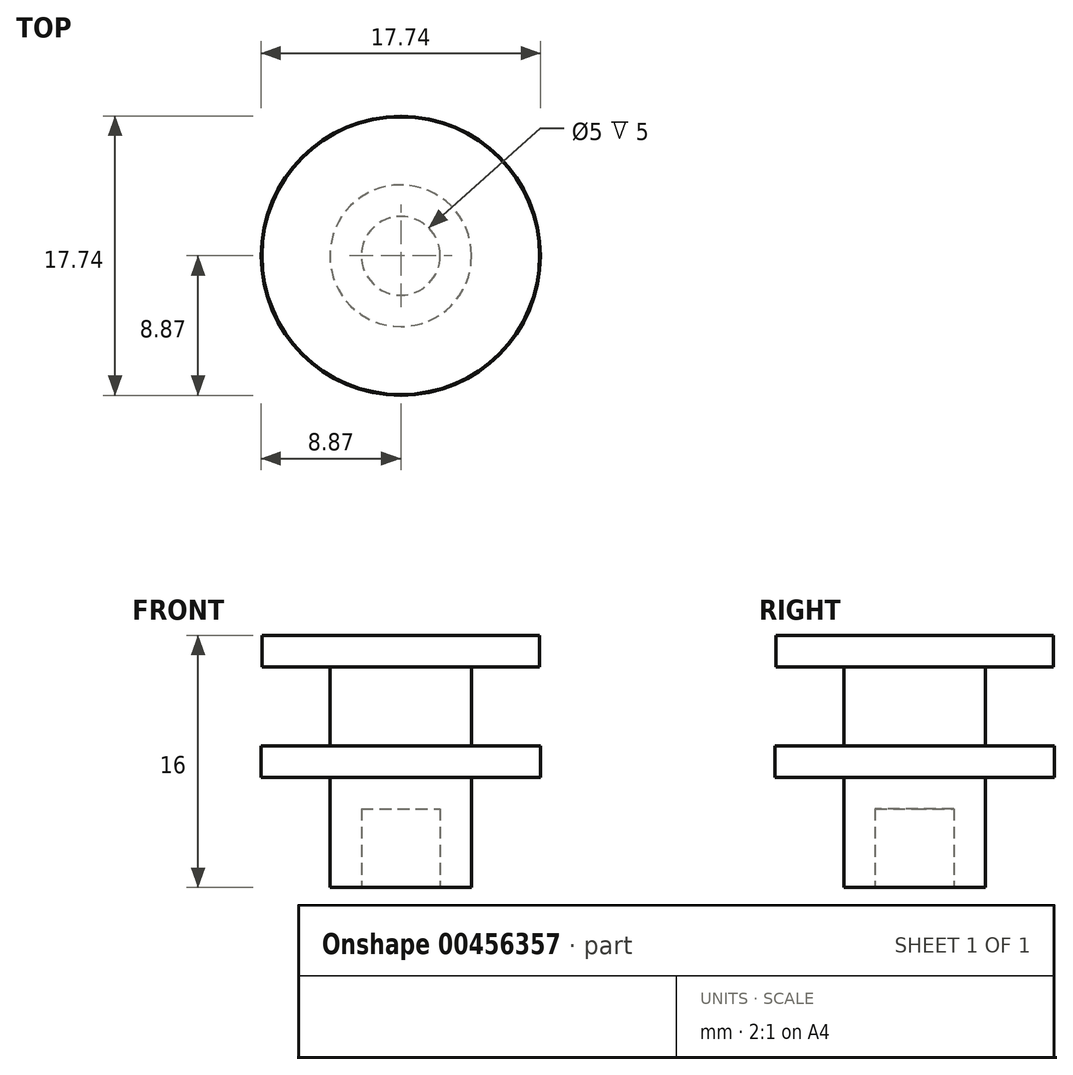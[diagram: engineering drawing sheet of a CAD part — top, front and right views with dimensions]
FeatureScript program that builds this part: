
annotation { "Feature Type Name" : "Feature", "Feature Type Description" : "" }
export const myFeature = defineFeature(function(context is Context, id is Id, definition is map)
    precondition{}
    {
        {
            var Q0;
            Q0=qCreatedBy(makeId("Front.planeOp"),FACE);
            var sketch = newSketch(context, id + "F0", { "sketchPlane" : qUnion([Q0])});
            skLineSegment(sketch, "E0", {"start": v(0, 0) * mm, "end": v(0, 9) * mm});
            skLineSegment(sketch, "E1", {"start": v(0, 9) * mm, "end": v(-8.82, 9) * mm});
            skLineSegment(sketch, "E2", {"start": v(-8.82, 9) * mm, "end": v(-8.82, 7) * mm});
            skLineSegment(sketch, "E3", {"start": v(-8.82, 7) * mm, "end": v(-4.5, 7) * mm});
            skLineSegment(sketch, "E4", {"start": v(-4.5, 7) * mm, "end": v(-4.5, 2) * mm});
            skLineSegment(sketch, "E5", {"start": v(-4.5, 2) * mm, "end": v(-8.87, 2) * mm});
            skLineSegment(sketch, "E6", {"start": v(-8.87, 2) * mm, "end": v(-8.87, 0) * mm});
            skLineSegment(sketch, "E7", {"start": v(-8.87, 0) * mm, "end": v(-4.5, 0) * mm});
            skLineSegment(sketch, "E8", {"start": v(-4.5, 0) * mm, "end": v(-4.5, -7) * mm});
            skLineSegment(sketch, "E9", {"start": v(-4.5, -7) * mm, "end": v(-2.5, -7) * mm});
            skLineSegment(sketch, "E10", {"start": v(-2.5, -7) * mm, "end": v(-2.5, -2) * mm});
            skLineSegment(sketch, "E11", {"start": v(-2.5, -2) * mm, "end": v(0, -2) * mm});
            skLineSegment(sketch, "E12", {"start": v(0, -2) * mm, "end": v(0, 0) * mm});
            skLineSegment(sketch, "E13", {"start": v(-0.44, 0) * mm, "end": v(-0.44, -2) * mm, "construction": true});
            skLineSegment(sketch, "E14", {"start": v(-4.5, 4.5) * mm, "end": v(0, 4.5) * mm, "construction": true});
            skSolve(sketch);
        }
        {
            var Q0;
            Q0=makeQuery(id+"F0.imprint","IMPRINT",FACE,{"disambiguationData":[TD([[makeQuery(id+"F0.imprint","IMPRINT",EDGE,{"derivedFrom":sQuery(id+"F0.wireOp",EDGE,"E0")}),1.0]])]});
            var Q1;
            Q1=sQuery(id+"F0.wireOp",EDGE,"E0");
            revolve(context, id + "F1", {"entities" : qUnion([Q0]), "axis" : qUnion([Q1]), "revolveType" : RevolveType.FULL});
        }
    });
